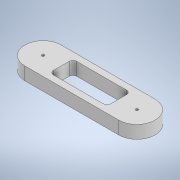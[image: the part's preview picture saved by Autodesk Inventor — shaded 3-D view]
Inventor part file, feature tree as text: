
AUTODESK INVENTOR PART (.ipt)
format: ipt  version: 2021 (Build 250183000, 183)  size: 200,192 bytes
history: native  units: mm
features: sketch x13, extrude x11, fillet x4
ambient origin geometry x8: Origin, YZ Plane, XZ Plane, XY Plane, X Axis, Y Axis, Z Axis, Center Point
bodies: Solid1 (feature_tree)
feature tree (28):
  extrude  "Extrusion1"  Depth=46.398mm
  extrude  "Extrusion2"  Depth=25.0mm TaperAngle=0.0deg
  extrude  "Extrusion3"  Depth=35.0mm
  extrude  "Extrusion4"  Depth=0.5mm TaperAngle=0.0deg
  extrude  "Extrusion5"  Depth=3.1mm
  extrude  "Extrusion6"  Depth=20.0mm TaperAngle=0.0deg
  extrude  "Extrusion7"  Depth=20.1mm
  extrude  "Extrusion8"  Depth=7.0mm
  sketch  "Sketch10"  dims[d22=2.0mm d23=2.0mm]
  extrude  "Extrusion9"  Depth=2.0mm
  extrude  "Extrusion10"  Depth=7.0mm
  extrude  "Extrusion11"  Depth=10.1mm
  fillet  "Fillet3"  Radius=10.1mm
  fillet  "Fillet4"  Radius=8.5mm
  fillet  "Fillet5"  Radius=8.5mm
  fillet  "Fillet6"  Radius=8.5mm
  sketch  "Sketch14"  dims[d39=23.199mm d40=15.0mm d41=15.0mm d42=19.75mm d43=0.0mm d44=5.0mm d45=5.0mm d46=5.0mm d47=5.0mm]
  sketch  "Sketch1"  dims[d0=120.0mm d1=46.398mm]
  sketch  "Sketch2"  dims[d2=25.0mm d3=0.0mm d4=25.0mm d5=0.0mm]
  sketch  "Sketch3"  dims[d6=35.0mm d7=35.0mm]
  sketch  "Sketch4"  dims[d8=8.0mm d9=0.0mm d10=0.5mm d11=0.0mm]
  sketch  "Sketch5"  dims[d12=0.5mm d13=0.0mm d14=3.1mm]
  sketch  "Sketch6"  dims[d15=3.1mm d16=20.0mm d17=0.0mm]
  sketch  "Sketch7"  dims[d18=20.1mm d19=20.1mm]
  sketch  "Sketch8"  dims[d20=7.0mm d21=7.0mm]
  sketch  "Sketch11"  dims[d24=7.0mm d25=7.0mm]
  sketch  "Sketch12"  dims[d26=2.0mm d27=2.0mm d28=10.1mm d29=0.0mm d30=8.5mm d31=0.0mm d34=8.5mm d35=0.0mm d36=8.5mm d37=0.0mm]
  sketch  "Sketch13"  dims[d38=23.199mm]
